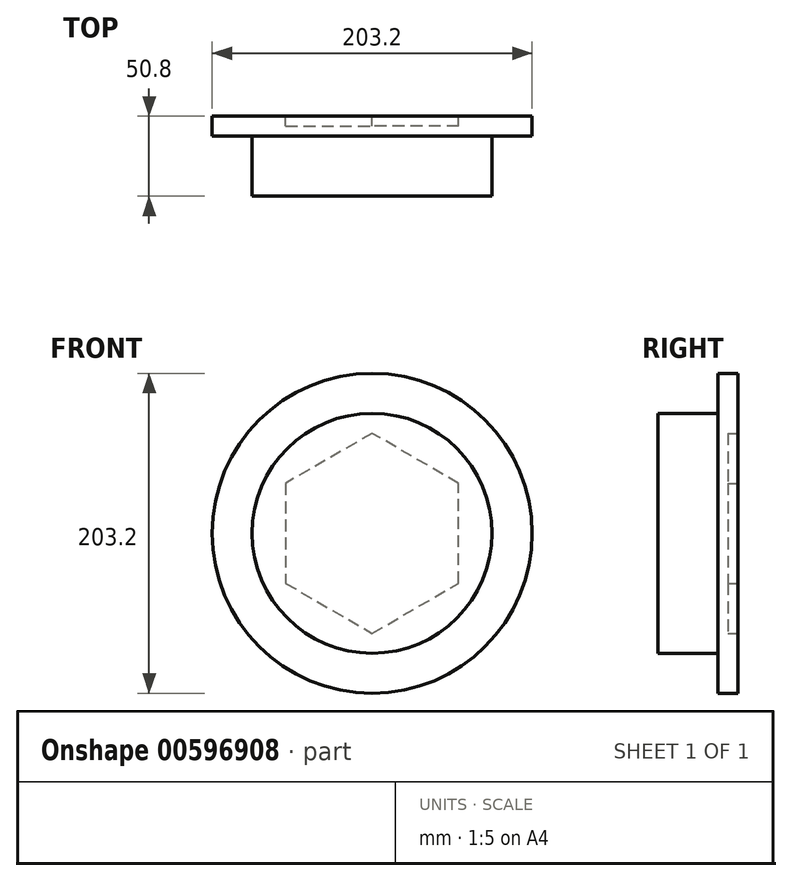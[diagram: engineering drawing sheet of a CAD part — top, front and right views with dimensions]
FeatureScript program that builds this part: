
annotation { "Feature Type Name" : "Feature", "Feature Type Description" : "" }
export const myFeature = defineFeature(function(context is Context, id is Id, definition is map)
    precondition{}
    {
        {
            var Q0;
            Q0=qCreatedBy(makeId("Top.planeOp"),FACE);
            var sketch = newSketch(context, id + "F0", { "sketchPlane" : qUnion([Q0])});
            skLineSegment(sketch, "E0", {"start": v(0, 0) * mm, "end": v(0, 50.8) * mm});
            skLineSegment(sketch, "E1", {"start": v(0, 50.8) * mm, "end": v(101.6, 50.8) * mm});
            skLineSegment(sketch, "E2", {"start": v(101.6, 50.8) * mm, "end": v(101.6, 38.1) * mm});
            skLineSegment(sketch, "E3", {"start": v(101.6, 38.1) * mm, "end": v(76.2, 38.1) * mm});
            skLineSegment(sketch, "E4", {"start": v(76.2, 38.1) * mm, "end": v(76.2, 0) * mm});
            skLineSegment(sketch, "E5", {"start": v(76.2, 0) * mm, "end": v(0, 0) * mm});
            skSolve(sketch);
        }
        {
            var Q0;
            Q0=makeQuery(id+"F0.imprint","IMPRINT",FACE,{"disambiguationData":[TD([[makeQuery(id+"F0.imprint","IMPRINT",EDGE,{"derivedFrom":sQuery(id+"F0.wireOp",EDGE,"E0")}),-1.0]])]});
            var Q1;
            Q1=sQuery(id+"F0.wireOp",EDGE,"E0");
            revolve(context, id + "F1", {"entities" : qUnion([Q0]), "axis" : qUnion([Q1]), "revolveType" : RevolveType.FULL});
        }
        {
            var Q0;
            Q0=makeQuery(id+"F1.opRevolve","SWEPT_FACE",FACE,{"disambiguationData":[OSD([sQuery(id+"F0.wireOp",EDGE,"E1")])]});
            var sketch = newSketch(context, id + "F2", { "sketchPlane" : qUnion([Q0])});
            skCircle(sketch, "E6.cCircle", {"center": v(0, 0) * mm, "radius": 63.5 * mm, "construction": true});
            skLineSegment(sketch, "E6.0", {"start": v(55, -31.75) * mm, "end": v(0, -63.5) * mm});
            skLineSegment(sketch, "E6.1", {"start": v(0, -63.5) * mm, "end": v(-55, -31.75) * mm});
            skLineSegment(sketch, "E6.2", {"start": v(-55, -31.75) * mm, "end": v(-55, 31.75) * mm});
            skLineSegment(sketch, "E6.3", {"start": v(-55, 31.75) * mm, "end": v(0, 63.5) * mm});
            skLineSegment(sketch, "E6.4", {"start": v(0, 63.5) * mm, "end": v(55, 31.75) * mm});
            skLineSegment(sketch, "E6.5", {"start": v(55, 31.75) * mm, "end": v(55, -31.75) * mm});
            skLineSegment(sketch, "E7", {"start": v(0, 0) * mm, "end": v(0, 63.5) * mm, "construction": true});
            skSolve(sketch);
        }
        {
            var Q0;
            Q0=makeQuery(id+"F2.imprint","IMPRINT",FACE,{"disambiguationData":[TD([[makeQuery(id+"F2.imprint","IMPRINT",EDGE,{"derivedFrom":sQuery(id+"F2.wireOp",EDGE,"E6.0")}),-1.0]])]});
            extrude(context, id + "F3", {"entities" : qUnion([Q0]), "operationType" : NewBodyOperationType.REMOVE, "oppositeDirection" : true, "depth" : 6.35 * mm, "offsetDistance" : 25.4 * mm});
        }
    });
